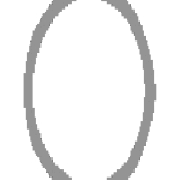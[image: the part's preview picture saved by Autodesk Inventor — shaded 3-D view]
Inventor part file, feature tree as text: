
AUTODESK INVENTOR PART (.ipt)
format: ipt  version: 2021 (Build 250183000, 183)  size: 110,080 bytes
history: native  units: in
note: dims shown in document units (in); Inventor stores cm internally (conversion verified against a paired STEP export)
features: other x4, sketch x3, plane x1
ambient origin geometry x8: Origin, YZ Plane, XZ Plane, XY Plane, X Axis, Y Axis, Z Axis, Center Point
bodies: Solid1 (feature_tree), Body (feature_tree)
feature tree (8):
  other  "Driven Length"
  other  "Frame Generator"
  other  "Start Plane"
  other  "End Plane"
  sketch  "Sketch"  dims[d2=12.431in d4=-0.0in d5=12.431in d6=0.12in d7=0.0in d8=90.0deg d9=12.431in]
  sketch  "Sketch2"  dims[d0=1.0in]
  plane  "Work Plane3"
  sketch  "Sketch3"  dims[d1=0.065in]
